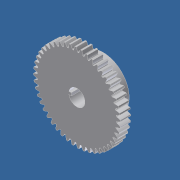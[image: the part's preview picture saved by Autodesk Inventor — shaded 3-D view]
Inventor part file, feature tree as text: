
AUTODESK INVENTOR PART (.ipt)
format: ipt  version: unknown  size: 580,608 bytes
history: native  units: in
note: dims shown in document units (in); Inventor stores cm internally (conversion verified against a paired STEP export)
features: extrude x3, sketch x3, imported_body x1
ambient origin geometry x8: Origin, YZ Plane, XZ Plane, XY Plane, X Axis, Y Axis, Z Axis, Center Point
bodies: Solid1 (feature_tree)
feature tree (7):
  imported_body  "Base1"
  extrude  "Extrusion5"  Depth=0.035in
  extrude  "Extrusion6"  Depth=1.0in TaperAngle=0.0deg
  extrude  "Extrusion7"  Depth=0.388in
  sketch  "Sketch1"  dims[d13=0.035in d14=0.035in]
  sketch  "Sketch4"  dims[d15=0.625in d16=0.0in d17=1.0in d18=0.0in]
  sketch  "Sketch5"  dims[d19=0.005in d20=0.0in d21=0.388in]
